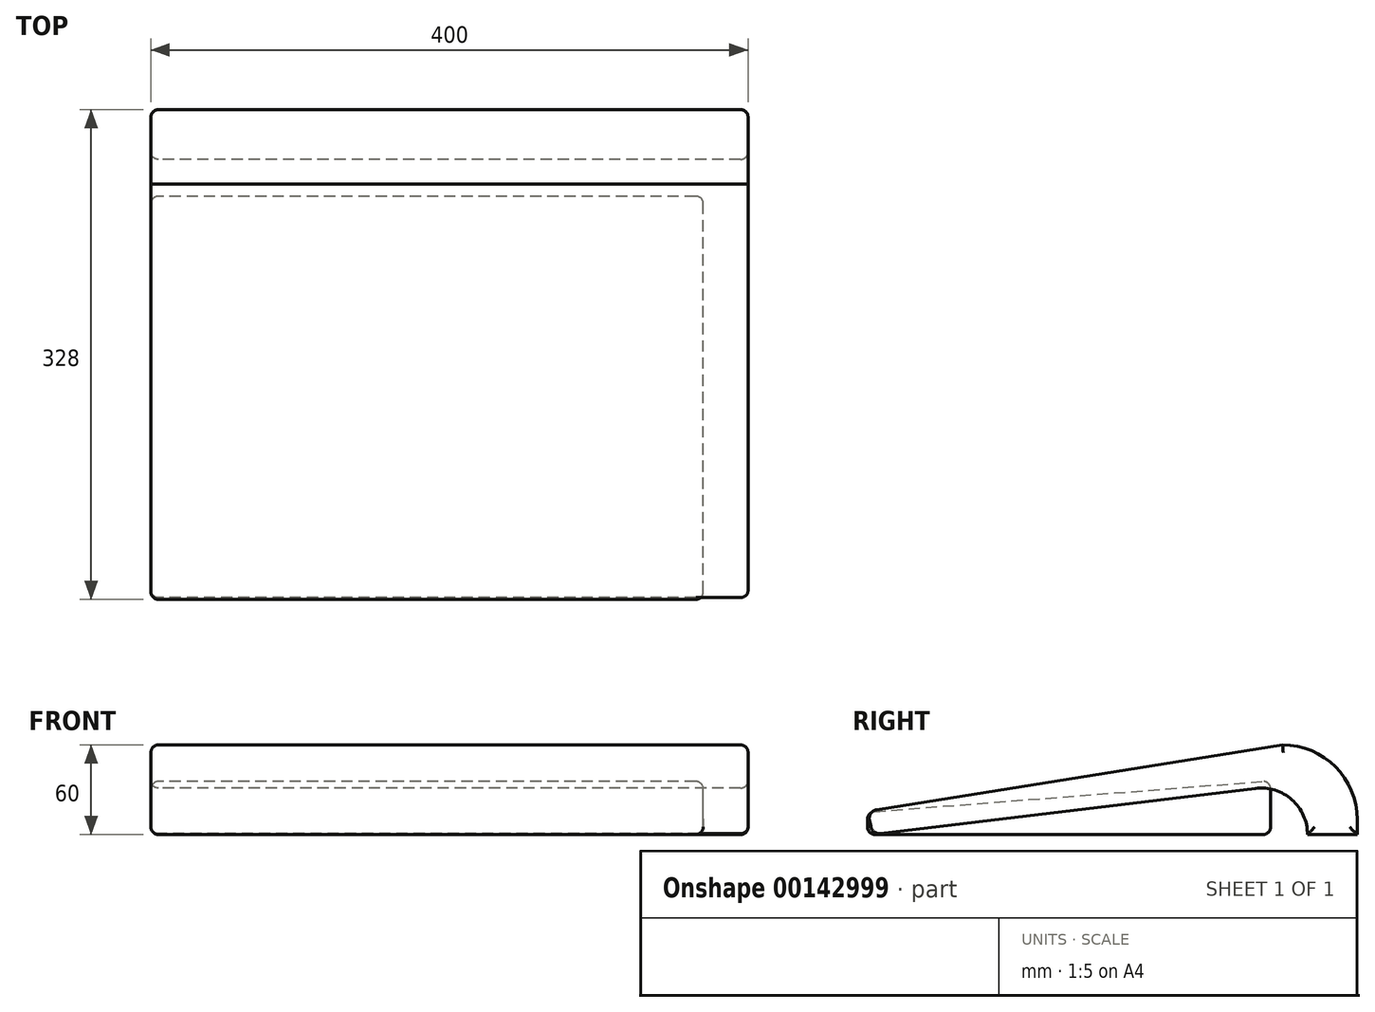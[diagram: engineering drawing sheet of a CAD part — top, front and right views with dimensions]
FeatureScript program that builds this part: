
annotation { "Feature Type Name" : "Feature", "Feature Type Description" : "" }
export const myFeature = defineFeature(function(context is Context, id is Id, definition is map)
    precondition{}
    {
        {
            var Q0;
            Q0=qCreatedBy(makeId("Right.planeOp"),FACE);
            var sketch = newSketch(context, id + "F0", { "sketchPlane" : qUnion([Q0])});
            skLineSegment(sketch, "E0.bottom", {"start": v(0, 0) * mm, "end": v(328, 0) * mm, "construction": true});
            skLineSegment(sketch, "E0.top", {"start": v(0, 60) * mm, "end": v(278, 60) * mm, "construction": true});
            skLineSegment(sketch, "E0.right", {"start": v(328, 0) * mm, "end": v(328, 10) * mm});
            skPoint(sketch, "E1.visualSharp", {"position": v(328, 60) * mm});
            skArc(sketch, "E1.filletArc", {"start": v(328, 10) * mm, "mid": v(313.36, 45.36) * mm, "end": v(278, 60) * mm});
            skPoint(sketch, "E2", {"position": v(0, -0.4) * mm});
            skPoint(sketch, "E3", {"position": v(259.88, 30.9) * mm});
            skLineSegment(sketch, "E4", {"start": v(8.77, 0.66) * mm, "end": v(259.88, 30.9) * mm});
            skArc(sketch, "E5", {"start": v(294.73, 0) * mm, "mid": v(284.25, 23.29) * mm, "end": v(259.88, 30.9) * mm});
            skLineSegment(sketch, "E6", {"start": v(0, 52.4) * mm, "end": v(0, 48.28) * mm});
            skLineSegment(sketch, "E7", {"start": v(328, 0) * mm, "end": v(294.73, 0) * mm});
            skPoint(sketch, "E8.visualSharp", {"position": v(0, 60) * mm});
            skLineSegment(sketch, "E9", {"start": v(278, 60) * mm, "end": v(6.23, 16.7) * mm});
            skLineSegment(sketch, "E10", {"start": v(1.3, 9.53) * mm, "end": v(2.18, 5.37) * mm});
            skPoint(sketch, "E11.visualSharp", {"position": v(0, 15.7) * mm});
            skArc(sketch, "E11.filletArc", {"start": v(6.23, 16.7) * mm, "mid": v(2.23, 14.17) * mm, "end": v(1.3, 9.53) * mm});
            skPoint(sketch, "E12.visualSharp", {"position": v(3.32, 0) * mm});
            skArc(sketch, "E12.filletArc", {"start": v(2.18, 5.37) * mm, "mid": v(4.56, 1.74) * mm, "end": v(8.77, 0.66) * mm});
            skSolve(sketch);
        }
        {
            var Q0;
            Q0 = qSketchRegion(id + "F0", true);
            extrude(context, id + "F1", {"entities" : qUnion([Q0]), "depth" : 400 * mm, "offsetDistance" : 25 * mm});
        }
        {
            var Q0;
            Q0=qCreatedBy(makeId("Right.planeOp"),FACE);
            var sketch = newSketch(context, id + "F2", { "sketchPlane" : qUnion([Q0])});
            skLineSegment(sketch, "E13.bottom", {"start": v(0, 0) * mm, "end": v(270, 0) * mm, "construction": true});
            skLineSegment(sketch, "E13.top", {"start": v(0, 36) * mm, "end": v(270, 36) * mm, "construction": true});
            skLineSegment(sketch, "E13.left", {"start": v(0, 0) * mm, "end": v(0, 36) * mm, "construction": true});
            skLineSegment(sketch, "E13.right", {"start": v(270, 0) * mm, "end": v(270, 36) * mm, "construction": true});
            skLineSegment(sketch, "E14", {"start": v(4.61, 15.36) * mm, "end": v(264.61, 35.58) * mm});
            skPoint(sketch, "E15.visualSharp", {"position": v(270, 0) * mm});
            skLineSegment(sketch, "E16", {"start": v(0, 10.37) * mm, "end": v(0, 5) * mm});
            skLineSegment(sketch, "E17", {"start": v(5, 0) * mm, "end": v(265, 0) * mm});
            skLineSegment(sketch, "E18", {"start": v(270, 5) * mm, "end": v(270, 30.6) * mm});
            skArc(sketch, "E19.filletArc", {"start": v(265, 0) * mm, "mid": v(268.54, 1.46) * mm, "end": v(270, 5) * mm});
            skPoint(sketch, "E20.visualSharp", {"position": v(270, 36) * mm});
            skArc(sketch, "E20.filletArc", {"start": v(270, 30.6) * mm, "mid": v(268.4, 34.27) * mm, "end": v(264.61, 35.58) * mm});
            skPoint(sketch, "E21.visualSharp", {"position": v(0, 15) * mm});
            skArc(sketch, "E21.filletArc", {"start": v(4.61, 15.36) * mm, "mid": v(1.33, 13.77) * mm, "end": v(0, 10.37) * mm});
            skPoint(sketch, "E22.visualSharp", {"position": v(0, 0) * mm});
            skArc(sketch, "E22.filletArc", {"start": v(0, 5) * mm, "mid": v(1.46, 1.46) * mm, "end": v(5, 0) * mm});
            skSolve(sketch);
        }
        {
            var Q0;
            Q0 = qSketchRegion(id + "F2", true);
            extrude(context, id + "F3", {"entities" : qUnion([Q0]), "depth" : 370 * mm, "offsetDistance" : 25 * mm});
        }
        {
            var Q0;
            Q0=makeQuery(id+"F1.opExtrude","CAP_FACE",FACE,{"disambiguationData":[OSD([sQuery(id+"F0.wireOp",EDGE,"E0.top"),sQuery(id+"F0.wireOp",EDGE,"E0.right"),sQuery(id+"F0.wireOp",EDGE,"E1.filletArc"),sQuery(id+"F0.wireOp",EDGE,"E4"),sQuery(id+"F0.wireOp",EDGE,"E5"),sQuery(id+"F0.wireOp",EDGE,"E6"),sQuery(id+"F0.wireOp",EDGE,"E7"),sQuery(id+"F0.wireOp",EDGE,"E8.filletArc"),sQuery(id+"F0.wireOp",EDGE,"e2a4e86c-21ea-41c2-861b-cea838dadea5.filletArc")])],"isStart":false});
            var Q1;
            Q1=makeQuery(id+"F1.opExtrude","CAP_FACE",FACE,{"disambiguationData":[OSD([sQuery(id+"F0.wireOp",EDGE,"E0.top"),sQuery(id+"F0.wireOp",EDGE,"E0.right"),sQuery(id+"F0.wireOp",EDGE,"E1.filletArc"),sQuery(id+"F0.wireOp",EDGE,"E4"),sQuery(id+"F0.wireOp",EDGE,"E5"),sQuery(id+"F0.wireOp",EDGE,"E6"),sQuery(id+"F0.wireOp",EDGE,"E7"),sQuery(id+"F0.wireOp",EDGE,"E8.filletArc"),sQuery(id+"F0.wireOp",EDGE,"e2a4e86c-21ea-41c2-861b-cea838dadea5.filletArc")])],"isStart":true});
            var Q2;
            Q2=makeQuery(id+"F3.opExtrude","CAP_FACE",FACE,{"disambiguationData":[OSD([sQuery(id+"F2.wireOp",EDGE,"E14"),sQuery(id+"F2.wireOp",EDGE,"E16"),sQuery(id+"F2.wireOp",EDGE,"E17"),sQuery(id+"F2.wireOp",EDGE,"E18"),sQuery(id+"F2.wireOp",EDGE,"E19.filletArc"),sQuery(id+"F2.wireOp",EDGE,"E20.filletArc"),sQuery(id+"F2.wireOp",EDGE,"E21.filletArc"),sQuery(id+"F2.wireOp",EDGE,"E22.filletArc")])],"isStart":false});
            var Q3;
            Q3=makeQuery(id+"F3.opExtrude","CAP_FACE",FACE,{"disambiguationData":[OSD([sQuery(id+"F2.wireOp",EDGE,"E14"),sQuery(id+"F2.wireOp",EDGE,"E16"),sQuery(id+"F2.wireOp",EDGE,"E17"),sQuery(id+"F2.wireOp",EDGE,"E18"),sQuery(id+"F2.wireOp",EDGE,"E19.filletArc"),sQuery(id+"F2.wireOp",EDGE,"E20.filletArc"),sQuery(id+"F2.wireOp",EDGE,"E21.filletArc"),sQuery(id+"F2.wireOp",EDGE,"E22.filletArc")])],"isStart":true});
            fillet(context, id + "F4", {"entities" : qUnion([Q0, Q1, Q2, Q3]), "radius" : 5 * mm, "tangentPropagation" : true, "allowEdgeOverflow" : false});
        }
    });
